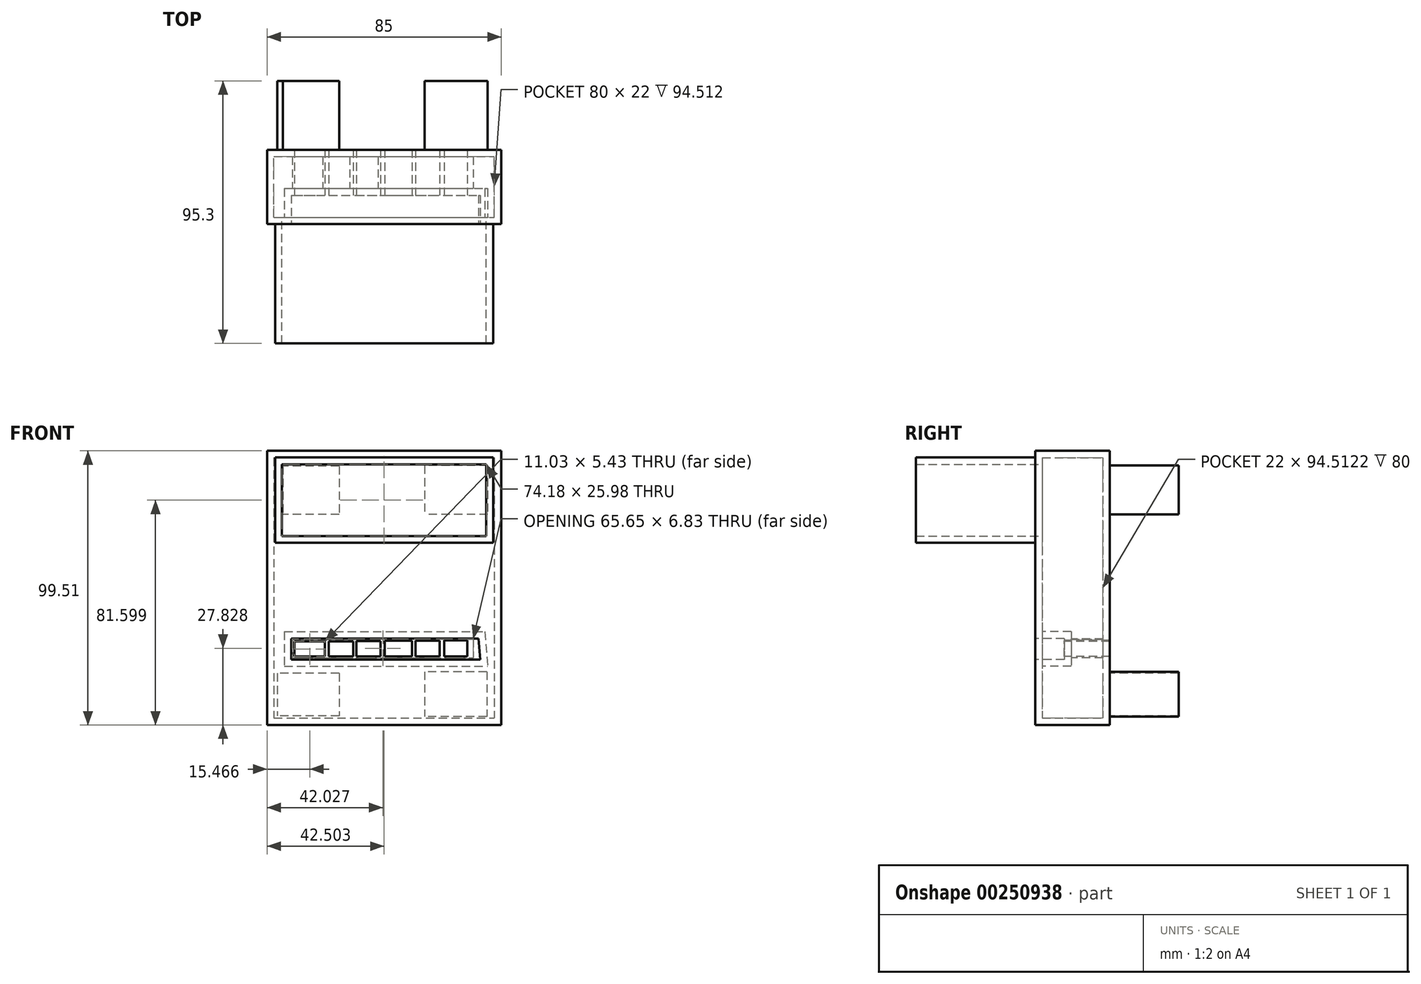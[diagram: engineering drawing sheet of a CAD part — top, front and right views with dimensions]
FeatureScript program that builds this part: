
annotation { "Feature Type Name" : "Feature", "Feature Type Description" : "" }
export const myFeature = defineFeature(function(context is Context, id is Id, definition is map)
    precondition{}
    {
        {
            var Q0;
            Q0=qCreatedBy(makeId("Front.planeOp"),FACE);
            var sketch = newSketch(context, id + "F0", { "sketchPlane" : qUnion([Q0])});
            skLineSegment(sketch, "E0.bottom", {"start": v(-39.06, 47.03) * mm, "end": v(45.94, 47.03) * mm});
            skLineSegment(sketch, "E0.top", {"start": v(-39.06, -52.48) * mm, "end": v(45.94, -52.48) * mm});
            skLineSegment(sketch, "E0.left", {"start": v(-39.06, 47.03) * mm, "end": v(-39.06, -52.48) * mm});
            skLineSegment(sketch, "E0.right", {"start": v(45.94, 47.03) * mm, "end": v(45.94, -52.48) * mm});
            skSolve(sketch);
        }
        {
            var Q0;
            Q0=makeQuery(id+"F0.imprint","IMPRINT",FACE,{"disambiguationData":[TD([[makeQuery(id+"F0.imprint","IMPRINT",EDGE,{"derivedFrom":sQuery(id+"F0.wireOp",EDGE,"E0.bottom")}),-1.0]])]});
            extrude(context, id + "F1", {"entities" : qUnion([Q0]), "depth" : 27 * mm});
        }
        {
            var Q0;
            Q0=makeQuery(id+"F1.opExtrude","CAP_FACE",FACE,{"disambiguationData":[OSD([sQuery(id+"F0.wireOp",EDGE,"E0.bottom"),sQuery(id+"F0.wireOp",EDGE,"E0.top"),sQuery(id+"F0.wireOp",EDGE,"E0.left"),sQuery(id+"F0.wireOp",EDGE,"E0.right")])],"isStart":false});
            var sketch = newSketch(context, id + "F2", { "sketchPlane" : qUnion([Q0])});
            skLineSegment(sketch, "E1", {"start": v(-30.3, -21.09) * mm, "end": v(37.7, -21.09) * mm});
            skLineSegment(sketch, "E2", {"start": v(-30.3, -21.09) * mm, "end": v(-30.3, -28.69) * mm});
            skLineSegment(sketch, "E3", {"start": v(-30.3, -28.69) * mm, "end": v(38.29, -28.69) * mm});
            skLineSegment(sketch, "E4", {"start": v(37.7, -21.09) * mm, "end": v(38.29, -28.69) * mm});
            skSolve(sketch);
        }
        {
            var Q0;
            Q0=makeQuery(id+"F2.imprint","IMPRINT",FACE,{"disambiguationData":[TD([[makeQuery(id+"F2.imprint","IMPRINT",EDGE,{"derivedFrom":sQuery(id+"F2.wireOp",EDGE,"E1")}),-1.0]])]});
            extrude(context, id + "F3", {"entities" : qUnion([Q0]), "operationType" : NewBodyOperationType.REMOVE, "oppositeDirection" : true, "depth" : 10.5 * mm});
        }
        {
            var Q0;
            Q0=makeQuery(id+"F3.boolean.opBoolean","COPY",FACE,{"derivedFrom":makeQuery(id+"F3.opExtrude","CAP_FACE",FACE,{"disambiguationData":[OSD([sQuery(id+"F2.wireOp",EDGE,"E1"),sQuery(id+"F2.wireOp",EDGE,"E2"),sQuery(id+"F2.wireOp",EDGE,"E3"),sQuery(id+"F2.wireOp",EDGE,"E4")])],"isStart":false})});
            var sketch = newSketch(context, id + "F4", { "sketchPlane" : qUnion([Q0])});
            skLineSegment(sketch, "E5.bottom", {"start": v(-27.36, -24) * mm, "end": v(-20.66, -24) * mm});
            skLineSegment(sketch, "E5.top", {"start": v(-27.36, -25.57) * mm, "end": v(-20.66, -25.57) * mm});
            skLineSegment(sketch, "E5.left", {"start": v(-27.36, -24) * mm, "end": v(-27.36, -25.57) * mm});
            skLineSegment(sketch, "E5.right", {"start": v(-20.66, -24) * mm, "end": v(-20.66, -25.57) * mm});
            skLineSegment(sketch, "E6.bottom", {"start": v(-16.3, -23.91) * mm, "end": v(-9.7, -23.91) * mm});
            skLineSegment(sketch, "E6.top", {"start": v(-16.3, -25.57) * mm, "end": v(-9.7, -25.57) * mm});
            skLineSegment(sketch, "E6.left", {"start": v(-16.3, -23.91) * mm, "end": v(-16.3, -25.57) * mm});
            skLineSegment(sketch, "E6.right", {"start": v(-9.7, -23.91) * mm, "end": v(-9.7, -25.57) * mm});
            skLineSegment(sketch, "E7.bottom", {"start": v(-6.56, -23.83) * mm, "end": v(0.92, -23.83) * mm});
            skLineSegment(sketch, "E7.top", {"start": v(-6.56, -25.57) * mm, "end": v(0.92, -25.57) * mm});
            skLineSegment(sketch, "E7.left", {"start": v(-6.56, -23.83) * mm, "end": v(-6.56, -25.57) * mm});
            skLineSegment(sketch, "E7.right", {"start": v(0.92, -23.83) * mm, "end": v(0.92, -25.57) * mm});
            skLineSegment(sketch, "E8.bottom", {"start": v(3.7, -25.57) * mm, "end": v(12.06, -25.57) * mm});
            skLineSegment(sketch, "E8.top", {"start": v(3.7, -23.74) * mm, "end": v(12.06, -23.74) * mm});
            skLineSegment(sketch, "E8.left", {"start": v(3.7, -25.57) * mm, "end": v(3.7, -23.74) * mm});
            skLineSegment(sketch, "E8.right", {"start": v(12.06, -25.57) * mm, "end": v(12.06, -23.74) * mm});
            skLineSegment(sketch, "E9.bottom", {"start": v(14.84, -23.74) * mm, "end": v(22.15, -23.74) * mm});
            skLineSegment(sketch, "E9.top", {"start": v(14.84, -25.57) * mm, "end": v(22.15, -25.57) * mm});
            skLineSegment(sketch, "E9.left", {"start": v(14.84, -23.74) * mm, "end": v(14.84, -25.57) * mm});
            skLineSegment(sketch, "E9.right", {"start": v(22.15, -23.74) * mm, "end": v(22.15, -25.57) * mm});
            skLineSegment(sketch, "E10.bottom", {"start": v(25.29, -23.74) * mm, "end": v(33.3, -23.74) * mm});
            skLineSegment(sketch, "E10.top", {"start": v(25.29, -25.57) * mm, "end": v(33.3, -25.57) * mm});
            skLineSegment(sketch, "E10.left", {"start": v(25.29, -23.74) * mm, "end": v(25.29, -25.57) * mm});
            skLineSegment(sketch, "E10.right", {"start": v(33.3, -23.74) * mm, "end": v(33.3, -25.57) * mm});
            skSolve(sketch);
        }
        {
            var Q0;
            Q0=makeQuery(id+"F4.imprint","IMPRINT",FACE,{"disambiguationData":[TD([[makeQuery(id+"F4.imprint","IMPRINT",EDGE,{"derivedFrom":sQuery(id+"F4.wireOp",EDGE,"E5.bottom")}),-1.0]])]});
            var Q1;
            Q1=makeQuery(id+"F4.imprint","IMPRINT",FACE,{"disambiguationData":[TD([[makeQuery(id+"F4.imprint","IMPRINT",EDGE,{"derivedFrom":sQuery(id+"F4.wireOp",EDGE,"E6.bottom")}),-1.0]])]});
            var Q2;
            Q2=makeQuery(id+"F4.imprint","IMPRINT",FACE,{"disambiguationData":[TD([[makeQuery(id+"F4.imprint","IMPRINT",EDGE,{"derivedFrom":sQuery(id+"F4.wireOp",EDGE,"E7.bottom")}),-1.0]])]});
            var Q3;
            Q3=makeQuery(id+"F4.imprint","IMPRINT",FACE,{"disambiguationData":[TD([[makeQuery(id+"F4.imprint","IMPRINT",EDGE,{"derivedFrom":sQuery(id+"F4.wireOp",EDGE,"E8.bottom")}),1.0]])]});
            var Q4;
            Q4=makeQuery(id+"F4.imprint","IMPRINT",FACE,{"disambiguationData":[TD([[makeQuery(id+"F4.imprint","IMPRINT",EDGE,{"derivedFrom":sQuery(id+"F4.wireOp",EDGE,"E9.bottom")}),-1.0]])]});
            var Q5;
            Q5=makeQuery(id+"F4.imprint","IMPRINT",FACE,{"disambiguationData":[TD([[makeQuery(id+"F4.imprint","IMPRINT",EDGE,{"derivedFrom":sQuery(id+"F4.wireOp",EDGE,"E10.bottom")}),-1.0]])]});
            extrude(context, id + "F5", {"entities" : qUnion([Q0, Q1, Q2, Q3, Q4, Q5]), "operationType" : NewBodyOperationType.REMOVE, "oppositeDirection" : true, "depth" : 25 * mm});
        }
        {
            var Q0;
            Q0=makeQuery(id+"F1.opExtrude","CAP_FACE",FACE,{"disambiguationData":[OSD([sQuery(id+"F0.wireOp",EDGE,"E0.bottom"),sQuery(id+"F0.wireOp",EDGE,"E0.top"),sQuery(id+"F0.wireOp",EDGE,"E0.left"),sQuery(id+"F0.wireOp",EDGE,"E0.right")])],"isStart":false});
            var sketch = newSketch(context, id + "F6", { "sketchPlane" : qUnion([Q0])});
            skLineSegment(sketch, "E11.bottom", {"start": v(-36.15, 44.61) * mm, "end": v(43.03, 44.61) * mm});
            skLineSegment(sketch, "E11.top", {"start": v(-36.15, 13.63) * mm, "end": v(43.03, 13.63) * mm});
            skLineSegment(sketch, "E11.left", {"start": v(-36.15, 44.61) * mm, "end": v(-36.15, 13.63) * mm});
            skLineSegment(sketch, "E11.right", {"start": v(43.03, 44.61) * mm, "end": v(43.03, 13.63) * mm});
            skSolve(sketch);
        }
        {
            var Q0;
            Q0=makeQuery(id+"F6.imprint","IMPRINT",FACE,{"disambiguationData":[TD([[makeQuery(id+"F6.imprint","IMPRINT",EDGE,{"derivedFrom":sQuery(id+"F6.wireOp",EDGE,"E11.bottom")}),-1.0]])]});
            extrude(context, id + "F7", {"entities" : qUnion([Q0]), "operationType" : NewBodyOperationType.ADD, "depth" : 43.3 * mm});
        }
        {
            var Q0;
            Q0=makeQuery(id+"F7.opExtrude","CAP_FACE",FACE,{"disambiguationData":[OSD([sQuery(id+"F6.wireOp",EDGE,"E11.bottom"),sQuery(id+"F6.wireOp",EDGE,"E11.top"),sQuery(id+"F6.wireOp",EDGE,"E11.left"),sQuery(id+"F6.wireOp",EDGE,"E11.right")])],"isStart":false});
            shell(context, id + "F8", {"entities" : qUnion([Q0]), "thickness" : 2.5 * mm});
        }
        {
            var Q0;
            Q0=makeQuery(id+"F1.opExtrude","CAP_FACE",FACE,{"disambiguationData":[OSD([sQuery(id+"F0.wireOp",EDGE,"E0.bottom"),sQuery(id+"F0.wireOp",EDGE,"E0.top"),sQuery(id+"F0.wireOp",EDGE,"E0.left"),sQuery(id+"F0.wireOp",EDGE,"E0.right")])],"isStart":true});
            var sketch = newSketch(context, id + "F9", { "sketchPlane" : qUnion([Q0])});
            skLineSegment(sketch, "E12.bottom", {"start": v(-41.02, 41.74) * mm, "end": v(-18.07, 41.74) * mm});
            skLineSegment(sketch, "E12.top", {"start": v(-41.02, 23.95) * mm, "end": v(-18.07, 23.95) * mm});
            skLineSegment(sketch, "E12.left", {"start": v(-41.02, 41.74) * mm, "end": v(-41.02, 23.95) * mm});
            skLineSegment(sketch, "E12.right", {"start": v(-18.07, 41.74) * mm, "end": v(-18.07, 23.95) * mm});
            skLineSegment(sketch, "E13.bottom", {"start": v(12.9, 41.45) * mm, "end": v(33.28, 41.45) * mm});
            skLineSegment(sketch, "E13.top", {"start": v(12.9, 23.95) * mm, "end": v(33.28, 23.95) * mm});
            skLineSegment(sketch, "E13.left", {"start": v(12.9, 41.45) * mm, "end": v(12.9, 23.95) * mm});
            skLineSegment(sketch, "E13.right", {"start": v(33.28, 41.45) * mm, "end": v(33.28, 23.95) * mm});
            skLineSegment(sketch, "E14.bottom", {"start": v(-40.74, -33.14) * mm, "end": v(-18.07, -33.14) * mm});
            skLineSegment(sketch, "E14.top", {"start": v(-40.74, -49.49) * mm, "end": v(-18.07, -49.49) * mm});
            skLineSegment(sketch, "E14.left", {"start": v(-40.74, -33.14) * mm, "end": v(-40.74, -49.49) * mm});
            skLineSegment(sketch, "E14.right", {"start": v(-18.07, -33.14) * mm, "end": v(-18.07, -49.49) * mm});
            skLineSegment(sketch, "E15.bottom", {"start": v(12.9, -33.7) * mm, "end": v(35.29, -33.7) * mm});
            skLineSegment(sketch, "E15.top", {"start": v(12.9, -49.2) * mm, "end": v(35.29, -49.2) * mm});
            skLineSegment(sketch, "E15.left", {"start": v(12.9, -33.7) * mm, "end": v(12.9, -49.2) * mm});
            skLineSegment(sketch, "E15.right", {"start": v(35.29, -33.7) * mm, "end": v(35.29, -49.2) * mm});
            skSolve(sketch);
        }
        {
            var Q0;
            Q0=makeQuery(id+"F9.imprint","IMPRINT",FACE,{"disambiguationData":[TD([[makeQuery(id+"F9.imprint","IMPRINT",EDGE,{"derivedFrom":sQuery(id+"F9.wireOp",EDGE,"E13.bottom")}),-1.0]])]});
            var Q1;
            Q1=makeQuery(id+"F9.imprint","IMPRINT",FACE,{"disambiguationData":[TD([[makeQuery(id+"F9.imprint","IMPRINT",EDGE,{"derivedFrom":sQuery(id+"F9.wireOp",EDGE,"E12.bottom")}),-1.0]])]});
            var Q2;
            Q2=makeQuery(id+"F9.imprint","IMPRINT",FACE,{"disambiguationData":[TD([[makeQuery(id+"F9.imprint","IMPRINT",EDGE,{"derivedFrom":sQuery(id+"F9.wireOp",EDGE,"E14.bottom")}),-1.0]])]});
            var Q3;
            Q3=makeQuery(id+"F9.imprint","IMPRINT",FACE,{"disambiguationData":[TD([[makeQuery(id+"F9.imprint","IMPRINT",EDGE,{"derivedFrom":sQuery(id+"F9.wireOp",EDGE,"E15.bottom")}),-1.0]])]});
            extrude(context, id + "F10", {"entities" : qUnion([Q0, Q1, Q2, Q3]), "operationType" : NewBodyOperationType.ADD, "depth" : 25 * mm});
        }
        {
            var Q0;
            Q0=makeQuery(id+"F3.boolean.opBoolean","COPY",FACE,{"derivedFrom":makeQuery(id+"F3.opExtrude","CAP_FACE",FACE,{"disambiguationData":[OSD([sQuery(id+"F2.wireOp",EDGE,"E1"),sQuery(id+"F2.wireOp",EDGE,"E2"),sQuery(id+"F2.wireOp",EDGE,"E3"),sQuery(id+"F2.wireOp",EDGE,"E4")])],"isStart":false})});
            var sketch = newSketch(context, id + "F11", { "sketchPlane" : qUnion([Q0])});
            skLineSegment(sketch, "E16.bottom", {"start": v(-29.1, -22.17) * mm, "end": v(-18.08, -22.17) * mm});
            skLineSegment(sketch, "E16.top", {"start": v(-29.1, -27.6) * mm, "end": v(-18.08, -27.6) * mm});
            skLineSegment(sketch, "E16.left", {"start": v(-29.1, -22.17) * mm, "end": v(-29.1, -27.6) * mm});
            skLineSegment(sketch, "E16.right", {"start": v(-18.08, -22.17) * mm, "end": v(-18.08, -27.6) * mm});
            skLineSegment(sketch, "E17.bottom", {"start": v(-16.66, -22.17) * mm, "end": v(-7.76, -22.17) * mm});
            skLineSegment(sketch, "E17.top", {"start": v(-16.66, -27.6) * mm, "end": v(-7.76, -27.6) * mm});
            skLineSegment(sketch, "E17.left", {"start": v(-16.66, -22.17) * mm, "end": v(-16.66, -27.6) * mm});
            skLineSegment(sketch, "E17.right", {"start": v(-7.76, -22.17) * mm, "end": v(-7.76, -27.6) * mm});
            skLineSegment(sketch, "E18.bottom", {"start": v(-6.7, -21.99) * mm, "end": v(2.1, -21.99) * mm});
            skLineSegment(sketch, "E18.top", {"start": v(-6.7, -27.6) * mm, "end": v(2.1, -27.6) * mm});
            skLineSegment(sketch, "E18.left", {"start": v(-6.7, -21.99) * mm, "end": v(-6.7, -27.6) * mm});
            skLineSegment(sketch, "E18.right", {"start": v(2.1, -21.99) * mm, "end": v(2.1, -27.6) * mm});
            skLineSegment(sketch, "E19.bottom", {"start": v(3.7, -21.9) * mm, "end": v(13.58, -21.9) * mm});
            skLineSegment(sketch, "E19.top", {"start": v(3.7, -27.6) * mm, "end": v(13.58, -27.6) * mm});
            skLineSegment(sketch, "E19.left", {"start": v(3.7, -21.9) * mm, "end": v(3.7, -27.6) * mm});
            skLineSegment(sketch, "E19.right", {"start": v(13.58, -21.9) * mm, "end": v(13.58, -27.6) * mm});
            skLineSegment(sketch, "E20.bottom", {"start": v(14.84, -21.9) * mm, "end": v(23.63, -21.9) * mm});
            skLineSegment(sketch, "E20.top", {"start": v(14.84, -27.6) * mm, "end": v(23.63, -27.6) * mm});
            skLineSegment(sketch, "E20.left", {"start": v(14.84, -21.9) * mm, "end": v(14.84, -27.6) * mm});
            skLineSegment(sketch, "E20.right", {"start": v(23.63, -21.9) * mm, "end": v(23.63, -27.6) * mm});
            skLineSegment(sketch, "E21.bottom", {"start": v(25.29, -21.72) * mm, "end": v(33.68, -21.72) * mm});
            skLineSegment(sketch, "E21.top", {"start": v(25.29, -27.6) * mm, "end": v(33.68, -27.6) * mm});
            skLineSegment(sketch, "E21.left", {"start": v(25.29, -21.72) * mm, "end": v(25.29, -27.6) * mm});
            skLineSegment(sketch, "E21.right", {"start": v(33.68, -21.72) * mm, "end": v(33.68, -27.6) * mm});
            skSolve(sketch);
        }
        {
            var Q0;
            Q0=makeQuery(id+"F11.imprint","IMPRINT",FACE,{"disambiguationData":[TD([[makeQuery(id+"F11.imprint","IMPRINT",EDGE,{"derivedFrom":sQuery(id+"F11.wireOp",EDGE,"E16.bottom")}),-1.0]])]});
            var Q1;
            Q1=makeQuery(id+"F11.imprint","IMPRINT",FACE,{"disambiguationData":[TD([[makeQuery(id+"F11.imprint","IMPRINT",EDGE,{"derivedFrom":sQuery(id+"F11.wireOp",EDGE,"E17.bottom")}),-1.0]])]});
            var Q2;
            Q2=makeQuery(id+"F11.imprint","IMPRINT",FACE,{"disambiguationData":[TD([[makeQuery(id+"F11.imprint","IMPRINT",EDGE,{"derivedFrom":sQuery(id+"F11.wireOp",EDGE,"E18.bottom")}),-1.0]])]});
            var Q3;
            {var subQ4=sQuery(id+"F11.wireOp",EDGE,"E19.bottom");Q3=makeQuery(id+"F11.imprint","IMPRINT",FACE,{"disambiguationData":[TD([[makeQuery(id+"F11.imprint","IMPRINT",EDGE,{"derivedFrom":subQ4}),-1.0]])]});}
            var Q4;
            {var subQ4=sQuery(id+"F11.wireOp",EDGE,"E20.bottom");Q4=makeQuery(id+"F11.imprint","IMPRINT",FACE,{"disambiguationData":[TD([[makeQuery(id+"F11.imprint","IMPRINT",EDGE,{"derivedFrom":subQ4}),-1.0]])]});}
            var Q5;
            {var subQ4=sQuery(id+"F11.wireOp",EDGE,"E21.bottom");Q5=makeQuery(id+"F11.imprint","IMPRINT",FACE,{"disambiguationData":[TD([[makeQuery(id+"F11.imprint","IMPRINT",EDGE,{"derivedFrom":subQ4}),-1.0]])]});}
            extrude(context, id + "F12", {"entities" : qUnion([Q0, Q1, Q2, Q3, Q4, Q5]), "operationType" : NewBodyOperationType.REMOVE, "oppositeDirection" : true, "depth" : 25 * mm});
        }
    });
